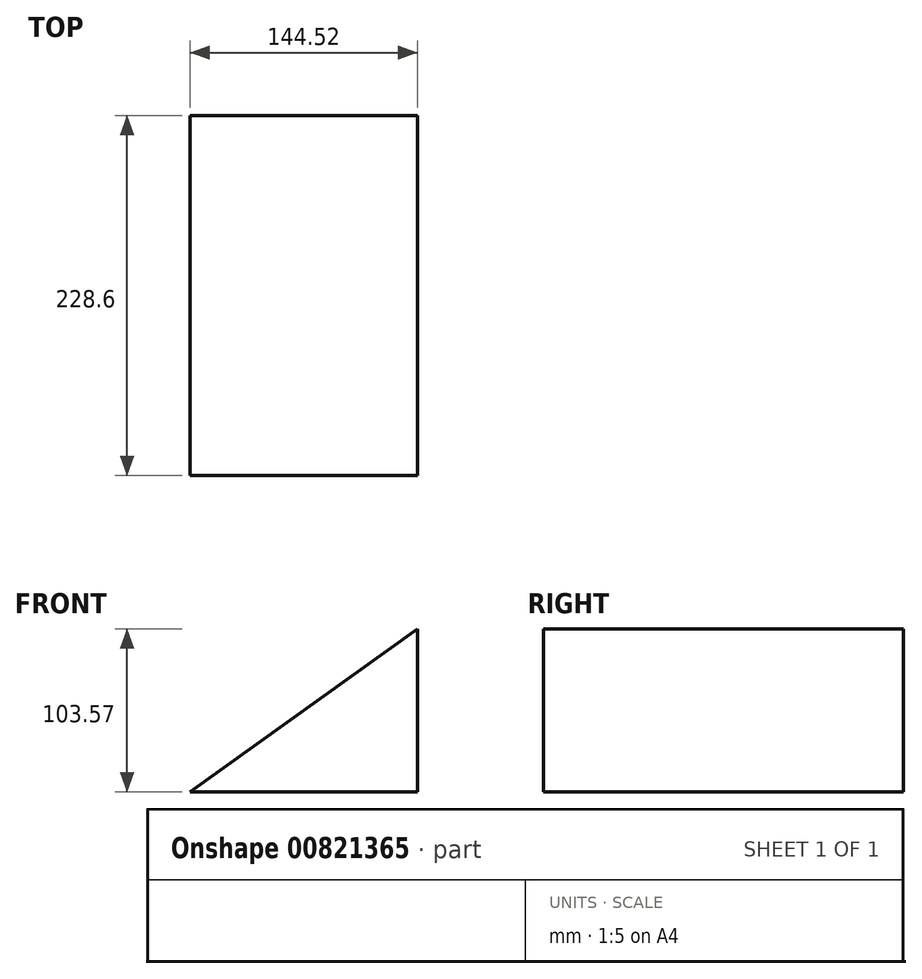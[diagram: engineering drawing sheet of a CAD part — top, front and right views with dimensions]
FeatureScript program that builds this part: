
annotation { "Feature Type Name" : "Feature", "Feature Type Description" : "" }
export const myFeature = defineFeature(function(context is Context, id is Id, definition is map)
    precondition{}
    {
        {
            var Q0;
            Q0=qCreatedBy(makeId("Front.planeOp"),FACE);
            var sketch = newSketch(context, id + "F0", { "sketchPlane" : qUnion([Q0])});
            skLineSegment(sketch, "E0", {"start": v(0, 0) * mm, "end": v(144.52, 103.57) * mm});
            skLineSegment(sketch, "E1", {"start": v(144.52, 103.57) * mm, "end": v(144.52, 0) * mm});
            skLineSegment(sketch, "E2", {"start": v(144.52, 0) * mm, "end": v(0, 0) * mm});
            skSolve(sketch);
        }
        {
            var Q0;
            Q0=makeQuery(id+"F0.imprint","IMPRINT",FACE,{"disambiguationData":[TD([[makeQuery(id+"F0.imprint","IMPRINT",EDGE,{"derivedFrom":sQuery(id+"F0.wireOp",EDGE,"E0")}),-1.0]])]});
            extrude(context, id + "F1", {"entities" : qUnion([Q0]), "depth" : 228.6 * mm, "offsetDistance" : 25.4 * mm});
        }
    });
